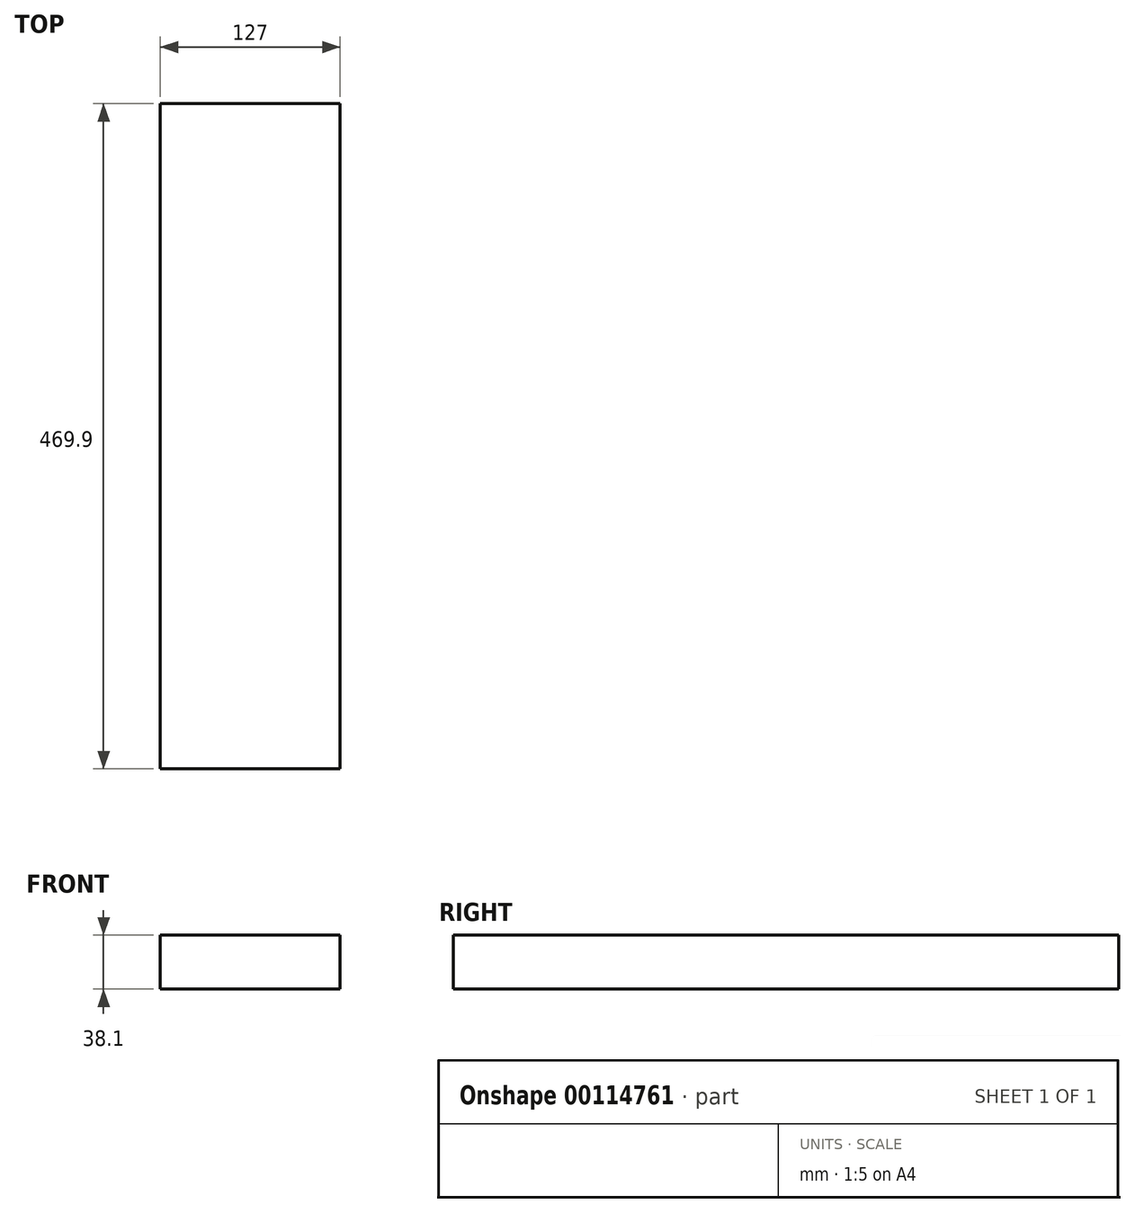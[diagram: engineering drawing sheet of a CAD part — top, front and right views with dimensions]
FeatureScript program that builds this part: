
annotation { "Feature Type Name" : "Feature", "Feature Type Description" : "" }
export const myFeature = defineFeature(function(context is Context, id is Id, definition is map)
    precondition{}
    {
        {
            var Q0;
            Q0=qCreatedBy(makeId("Top.planeOp"),FACE);
            var sketch = newSketch(context, id + "F0", { "sketchPlane" : qUnion([Q0])});
            skLineSegment(sketch, "E0.bottom", {"start": v(0, 0) * mm, "end": v(127, 0) * mm});
            skLineSegment(sketch, "E0.top", {"start": v(0, 469.9) * mm, "end": v(127, 469.9) * mm});
            skLineSegment(sketch, "E0.left", {"start": v(0, 0) * mm, "end": v(0, 469.9) * mm});
            skLineSegment(sketch, "E0.right", {"start": v(127, 0) * mm, "end": v(127, 469.9) * mm});
            skSolve(sketch);
        }
        {
            var Q0;
            Q0=qSketchRegion(id+"F0",true);
            extrude(context, id + "F1", {"entities" : qUnion([Q0]), "depth" : 38.1 * mm});
        }
    });
